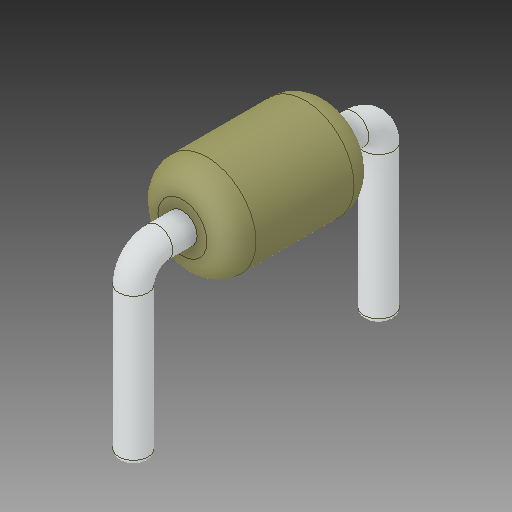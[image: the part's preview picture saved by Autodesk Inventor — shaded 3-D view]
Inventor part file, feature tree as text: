
AUTODESK INVENTOR PART (.ipt)
format: ipt  version: 2019 (Build 230136000, 136)  size: 154,112 bytes
history: mixed  units: mm
features: other x1, fillet x1, imported_body x1
ambient origin geometry x8: Origin, YZ Plane, XZ Plane, XY Plane, X Axis, Y Axis, Z Axis, Center Point
bodies: Body1 (imported_parasolid)
feature tree (3):
  other  "Твердое тело1"
  fillet  "Fillet2"  [1 undecoded]
  imported_body  NMx_Import_Brep_tag  [imported B-rep: ~15 faces, bbox_mm=[1.0, 3.8, 5.6]]
note: 1 required parameter value undecoded (feature->parameter linkage not recoverable at this tier; creation-order binding heuristic only, values carry confidence <= 0.55)
